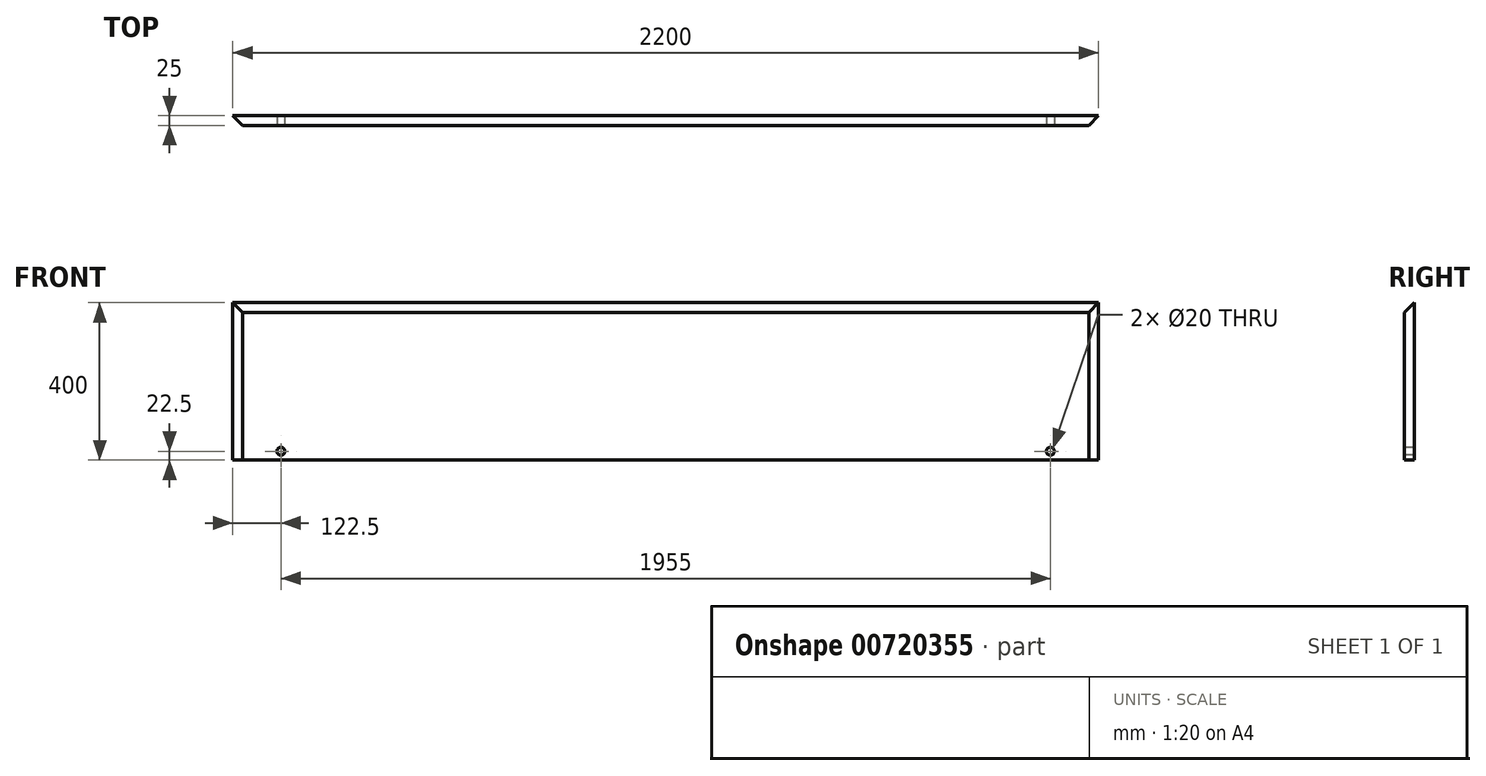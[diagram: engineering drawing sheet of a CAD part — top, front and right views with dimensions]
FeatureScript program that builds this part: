
annotation { "Feature Type Name" : "Feature", "Feature Type Description" : "" }
export const myFeature = defineFeature(function(context is Context, id is Id, definition is map)
    precondition{}
    {
        {
            var Q0;
            Q0=qCreatedBy(makeId("Front.planeOp"),FACE);
            var sketch = newSketch(context, id + "F0", { "sketchPlane" : qUnion([Q0])});
            skLineSegment(sketch, "E0.bottom", {"start": v(1100, 200) * mm, "end": v(-1100, 200) * mm});
            skLineSegment(sketch, "E0.top", {"start": v(1100, -200) * mm, "end": v(-1100, -200) * mm});
            skLineSegment(sketch, "E0.left", {"start": v(1100, 200) * mm, "end": v(1100, -200) * mm});
            skLineSegment(sketch, "E0.right", {"start": v(-1100, 200) * mm, "end": v(-1100, -200) * mm});
            skPoint(sketch, "E0.middle", {"position": v(0, 0) * mm});
            skSolve(sketch);
        }
        {
            var Q0;
            Q0=makeQuery(id+"F0.imprint","IMPRINT",FACE,{"disambiguationData":[TD([[makeQuery(id+"F0.imprint","IMPRINT",EDGE,{"derivedFrom":sQuery(id+"F0.wireOp",EDGE,"E0.bottom")}),1.0]])]});
            extrude(context, id + "F1", {"entities" : qUnion([Q0]), "depth" : 25 * mm, "offsetDistance" : 25 * mm});
        }
        {
            var Q0;
            Q0=makeQuery(id+"F1.opExtrude","CAP_FACE",FACE,{"disambiguationData":[OSD([sQuery(id+"F0.wireOp",EDGE,"E0.bottom"),sQuery(id+"F0.wireOp",EDGE,"E0.top"),sQuery(id+"F0.wireOp",EDGE,"E0.left"),sQuery(id+"F0.wireOp",EDGE,"E0.right")])],"isStart":false});
            var sketch = newSketch(context, id + "F2", { "sketchPlane" : qUnion([Q0])});
            skCircle(sketch, "E1", {"center": v(977.5, -77.5) * mm, "radius": 10 * mm});
            skSolve(sketch);
        }
        {
            var Q0;
            Q0 = qSketchRegion(id + "F2", true);
            extrude(context, id + "F3", {"entities" : qUnion([Q0]), "operationType" : NewBodyOperationType.REMOVE, "oppositeDirection" : true, "depth" : 25 * mm, "offsetDistance" : 25 * mm});
        }
        {
            var Q0;
            Q0=makeQuery(id+"F1.opExtrude","CAP_FACE",FACE,{"disambiguationData":[OSD([sQuery(id+"F0.wireOp",EDGE,"E0.bottom"),sQuery(id+"F0.wireOp",EDGE,"E0.top"),sQuery(id+"F0.wireOp",EDGE,"E0.left"),sQuery(id+"F0.wireOp",EDGE,"E0.right")])],"isStart":false});
            var sketch = newSketch(context, id + "F4", { "sketchPlane" : qUnion([Q0])});
            skCircle(sketch, "E2", {"center": v(-977.5, -77.5) * mm, "radius": 10 * mm});
            skSolve(sketch);
        }
        {
            var Q0;
            Q0 = qSketchRegion(id + "F4", true);
            extrude(context, id + "F5", {"entities" : qUnion([Q0]), "operationType" : NewBodyOperationType.REMOVE, "oppositeDirection" : true, "depth" : 25 * mm, "offsetDistance" : 25 * mm});
        }
        {
            var Q0;
            Q0=makeQuery(id+"F1.opExtrude","SWEPT_FACE",FACE,{"disambiguationData":[OSD([sQuery(id+"F0.wireOp",EDGE,"E0.bottom")])]});
            extrude(context, id + "F6", {"entities" : qUnion([Q0]), "operationType" : NewBodyOperationType.ADD, "depth" : 100 * mm, "offsetDistance" : 25 * mm});
        }
        {
            var Q0;
            Q0=makeQuery(id+"F1.opExtrude","SWEPT_FACE",FACE,{"disambiguationData":[OSD([sQuery(id+"F0.wireOp",EDGE,"E0.top")])]});
            extrude(context, id + "F7", {"entities" : qUnion([Q0]), "operationType" : NewBodyOperationType.REMOVE, "oppositeDirection" : true, "depth" : 100 * mm, "offsetDistance" : 25 * mm});
        }
        {
            var Q0;
            {var subQ0=sQuery(id+"F0.wireOp",EDGE,"E0.right");var subQ1=sQuery(id+"F0.wireOp",EDGE,"E0.bottom");Q0=makeQuery(id+"F6.boolean.opBoolean","MERGE",EDGE,{"derivedFrom":[makeQuery(id+"F1.opExtrude","CAP_EDGE",EDGE,{"disambiguationData":[OSD([subQ0])],"isStart":false}),makeQuery(id+"F6.opExtrude","SWEPT_EDGE",EDGE,{"disambiguationData":[OSD([subQ1,subQ0]),TDD([makeQuery(id+"F1.opExtrude","CAP_VERTEX",VERTEX,{"disambiguationData":[OSD([subQ1,subQ0])],"isStart":false})])]})]});}
            var Q1;
            {var subQ0=sQuery(id+"F0.wireOp",EDGE,"E0.bottom");Q1=makeQuery(id+"F6.opExtrude","CAP_EDGE",EDGE,{"disambiguationData":[OSD([subQ0]),TDD([makeQuery(id+"F1.opExtrude","CAP_EDGE",EDGE,{"disambiguationData":[OSD([subQ0])],"isStart":false})])],"isStart":false});}
            var Q2;
            {var subQ0=sQuery(id+"F0.wireOp",EDGE,"E0.left");var subQ1=sQuery(id+"F0.wireOp",EDGE,"E0.bottom");Q2=makeQuery(id+"F6.boolean.opBoolean","MERGE",EDGE,{"derivedFrom":[makeQuery(id+"F1.opExtrude","CAP_EDGE",EDGE,{"disambiguationData":[OSD([subQ0])],"isStart":false}),makeQuery(id+"F6.opExtrude","SWEPT_EDGE",EDGE,{"disambiguationData":[OSD([subQ1,subQ0]),TDD([makeQuery(id+"F1.opExtrude","CAP_VERTEX",VERTEX,{"disambiguationData":[OSD([subQ1,subQ0])],"isStart":false})])]})]});}
            chamfer(context, id + "F8", {"entities" : qUnion([Q0, Q1, Q2]), "width" : 25 * mm, "tangentPropagation" : true});
        }
    });
